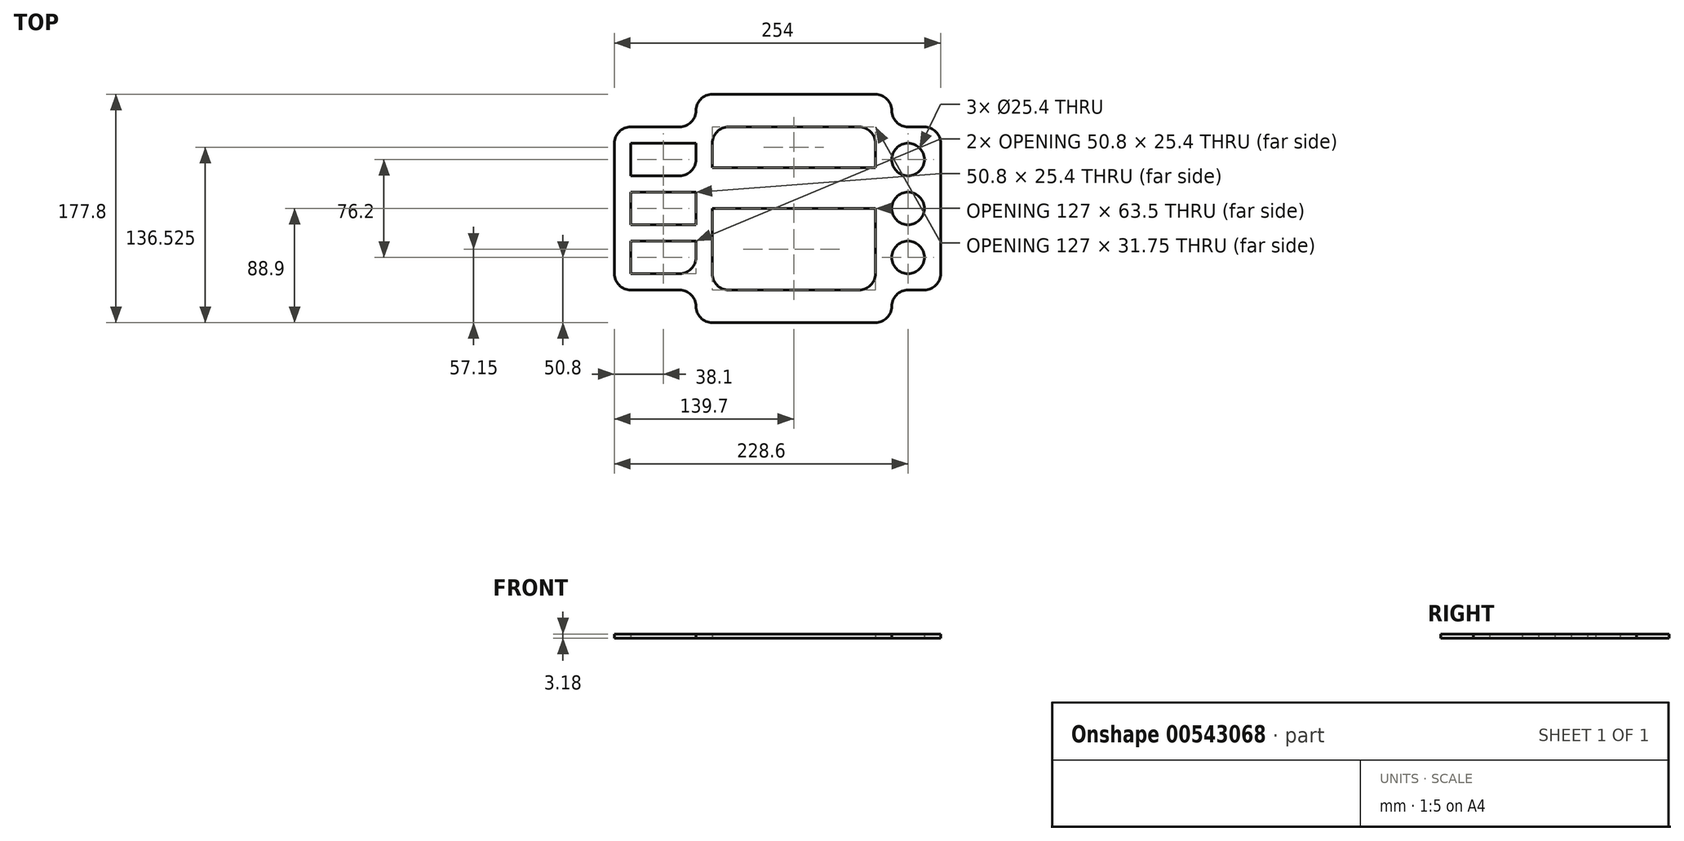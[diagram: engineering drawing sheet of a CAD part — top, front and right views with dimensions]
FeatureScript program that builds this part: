
annotation { "Feature Type Name" : "Feature", "Feature Type Description" : "" }
export const myFeature = defineFeature(function(context is Context, id is Id, definition is map)
    precondition{}
    {
        {
            var Q0;
            Q0=qCreatedBy(makeId("Top.planeOp"),FACE);
            var sketch = newSketch(context, id + "F0", { "sketchPlane" : qUnion([Q0])});
            skLineSegment(sketch, "E0", {"start": v(0, 12.7) * mm, "end": v(0, 12.7) * mm});
            skLineSegment(sketch, "E1", {"start": v(-12.7, 25.4) * mm, "end": v(-50.8, 25.4) * mm});
            skLineSegment(sketch, "E2", {"start": v(-63.5, 38.1) * mm, "end": v(-63.5, 139.7) * mm});
            skLineSegment(sketch, "E3", {"start": v(-50.8, 152.4) * mm, "end": v(-12.7, 152.4) * mm});
            skLineSegment(sketch, "E4", {"start": v(0, 165.1) * mm, "end": v(0, 165.1) * mm});
            skLineSegment(sketch, "E5", {"start": v(12.7, 177.8) * mm, "end": v(139.7, 177.8) * mm});
            skLineSegment(sketch, "E6", {"start": v(152.4, 165.1) * mm, "end": v(152.4, 165.1) * mm});
            skLineSegment(sketch, "E7", {"start": v(165.1, 152.4) * mm, "end": v(177.8, 152.4) * mm});
            skLineSegment(sketch, "E8", {"start": v(190.5, 139.7) * mm, "end": v(190.5, 38.1) * mm});
            skLineSegment(sketch, "E9", {"start": v(177.8, 25.4) * mm, "end": v(165.1, 25.4) * mm});
            skLineSegment(sketch, "E10", {"start": v(152.4, 12.7) * mm, "end": v(152.4, 12.7) * mm});
            skLineSegment(sketch, "E11", {"start": v(139.7, 0) * mm, "end": v(12.7, 0) * mm});
            skPoint(sketch, "E12.visualSharp", {"position": v(0, 25.4) * mm});
            skArc(sketch, "E12.filletArc", {"start": v(0, 12.7) * mm, "mid": v(-3.72, 21.68) * mm, "end": v(-12.7, 25.4) * mm});
            skPoint(sketch, "E13.visualSharp", {"position": v(0, 0) * mm});
            skArc(sketch, "E13.filletArc", {"start": v(0, 12.7) * mm, "mid": v(3.72, 3.72) * mm, "end": v(12.7, 0) * mm});
            skPoint(sketch, "E14.visualSharp", {"position": v(-63.5, 25.4) * mm});
            skArc(sketch, "E14.filletArc", {"start": v(-63.5, 38.1) * mm, "mid": v(-59.78, 29.12) * mm, "end": v(-50.8, 25.4) * mm});
            skPoint(sketch, "E15.visualSharp", {"position": v(-63.5, 152.4) * mm});
            skArc(sketch, "E15.filletArc", {"start": v(-50.8, 152.4) * mm, "mid": v(-59.78, 148.68) * mm, "end": v(-63.5, 139.7) * mm});
            skPoint(sketch, "E16.visualSharp", {"position": v(0, 152.4) * mm});
            skArc(sketch, "E16.filletArc", {"start": v(-12.7, 152.4) * mm, "mid": v(-3.72, 156.12) * mm, "end": v(0, 165.1) * mm});
            skPoint(sketch, "E17.visualSharp", {"position": v(0, 177.8) * mm});
            skArc(sketch, "E17.filletArc", {"start": v(12.7, 177.8) * mm, "mid": v(3.72, 174.08) * mm, "end": v(0, 165.1) * mm});
            skPoint(sketch, "E18.visualSharp", {"position": v(152.4, 177.8) * mm});
            skArc(sketch, "E18.filletArc", {"start": v(152.4, 165.1) * mm, "mid": v(148.68, 174.08) * mm, "end": v(139.7, 177.8) * mm});
            skLineSegment(sketch, "E19", {"start": v(165.1, 152.4) * mm, "end": v(165.1, 25.4) * mm, "construction": true});
            skCircle(sketch, "E20", {"center": v(165.1, 127) * mm, "radius": 12.7 * mm});
            skCircle(sketch, "E21", {"center": v(165.1, 88.9) * mm, "radius": 12.7 * mm});
            skCircle(sketch, "E22", {"center": v(165.1, 50.8) * mm, "radius": 12.7 * mm});
            skPoint(sketch, "E23.visualSharp", {"position": v(152.4, 25.4) * mm});
            skArc(sketch, "E23.filletArc", {"start": v(165.1, 25.4) * mm, "mid": v(156.12, 21.68) * mm, "end": v(152.4, 12.7) * mm});
            skPoint(sketch, "E24.visualSharp", {"position": v(152.4, 0) * mm});
            skArc(sketch, "E24.filletArc", {"start": v(139.7, 0) * mm, "mid": v(148.68, 3.72) * mm, "end": v(152.4, 12.7) * mm});
            skPoint(sketch, "E25.visualSharp", {"position": v(190.5, 25.4) * mm});
            skArc(sketch, "E25.filletArc", {"start": v(177.8, 25.4) * mm, "mid": v(186.78, 29.12) * mm, "end": v(190.5, 38.1) * mm});
            skPoint(sketch, "E26.visualSharp", {"position": v(190.5, 152.4) * mm});
            skArc(sketch, "E26.filletArc", {"start": v(190.5, 139.7) * mm, "mid": v(186.78, 148.68) * mm, "end": v(177.8, 152.4) * mm});
            skPoint(sketch, "E27.visualSharp", {"position": v(152.4, 152.4) * mm});
            skArc(sketch, "E27.filletArc", {"start": v(152.4, 165.1) * mm, "mid": v(156.12, 156.12) * mm, "end": v(165.1, 152.4) * mm});
            skLineSegment(sketch, "E28.bottom", {"start": v(25.4, 152.4) * mm, "end": v(127, 152.4) * mm});
            skLineSegment(sketch, "E28.top", {"start": v(12.7, 120.65) * mm, "end": v(139.7, 120.65) * mm});
            skLineSegment(sketch, "E28.left", {"start": v(12.7, 139.7) * mm, "end": v(12.7, 120.65) * mm});
            skLineSegment(sketch, "E28.right", {"start": v(139.7, 139.7) * mm, "end": v(139.7, 120.65) * mm});
            skPoint(sketch, "E29.visualSharp", {"position": v(12.7, 152.4) * mm});
            skArc(sketch, "E29.filletArc", {"start": v(25.4, 152.4) * mm, "mid": v(16.42, 148.68) * mm, "end": v(12.7, 139.7) * mm});
            skPoint(sketch, "E30.visualSharp", {"position": v(139.7, 152.4) * mm});
            skArc(sketch, "E30.filletArc", {"start": v(139.7, 139.7) * mm, "mid": v(135.98, 148.68) * mm, "end": v(127, 152.4) * mm});
            skLineSegment(sketch, "E31.bottom", {"start": v(12.7, 88.9) * mm, "end": v(139.7, 88.9) * mm});
            skLineSegment(sketch, "E31.top", {"start": v(25.4, 25.4) * mm, "end": v(127, 25.4) * mm});
            skLineSegment(sketch, "E31.left", {"start": v(12.7, 88.9) * mm, "end": v(12.7, 38.1) * mm});
            skLineSegment(sketch, "E31.right", {"start": v(139.7, 88.9) * mm, "end": v(139.7, 38.1) * mm});
            skPoint(sketch, "E32.visualSharp", {"position": v(12.7, 25.4) * mm});
            skArc(sketch, "E32.filletArc", {"start": v(12.7, 38.1) * mm, "mid": v(16.42, 29.12) * mm, "end": v(25.4, 25.4) * mm});
            skPoint(sketch, "E33.visualSharp", {"position": v(139.7, 25.4) * mm});
            skArc(sketch, "E33.filletArc", {"start": v(127, 25.4) * mm, "mid": v(135.98, 29.12) * mm, "end": v(139.7, 38.1) * mm});
            skLineSegment(sketch, "E34.bottom", {"start": v(-50.8, 139.7) * mm, "end": v(0, 139.7) * mm});
            skLineSegment(sketch, "E34.top", {"start": v(-50.8, 114.3) * mm, "end": v(-12.7, 114.3) * mm});
            skLineSegment(sketch, "E34.left", {"start": v(-50.8, 139.7) * mm, "end": v(-50.8, 114.3) * mm});
            skLineSegment(sketch, "E34.right", {"start": v(0, 139.7) * mm, "end": v(0, 127) * mm});
            skLineSegment(sketch, "E35.bottom", {"start": v(-50.8, 101.6) * mm, "end": v(0, 101.6) * mm});
            skLineSegment(sketch, "E35.top", {"start": v(-50.8, 76.2) * mm, "end": v(0, 76.2) * mm});
            skLineSegment(sketch, "E35.left", {"start": v(-50.8, 101.6) * mm, "end": v(-50.8, 76.2) * mm});
            skLineSegment(sketch, "E35.right", {"start": v(0, 101.6) * mm, "end": v(0, 76.2) * mm});
            skLineSegment(sketch, "E36", {"start": v(-50.8, 88.9) * mm, "end": v(0, 88.9) * mm, "construction": true});
            skLineSegment(sketch, "E37.MirrorCS", {"start": v(-50.8, 38.1) * mm, "end": v(-12.7, 38.1) * mm});
            skLineSegment(sketch, "E38.MirrorCS", {"start": v(-50.8, 38.1) * mm, "end": v(-50.8, 63.5) * mm});
            skLineSegment(sketch, "E39.MirrorCS", {"start": v(-50.8, 63.5) * mm, "end": v(0, 63.5) * mm});
            skLineSegment(sketch, "E40.MirrorCS", {"start": v(0, 50.8) * mm, "end": v(0, 63.5) * mm});
            skPoint(sketch, "E41.visualSharp", {"position": v(0, 114.3) * mm});
            skArc(sketch, "E41.filletArc", {"start": v(-12.7, 114.3) * mm, "mid": v(-3.72, 118.02) * mm, "end": v(0, 127) * mm});
            skPoint(sketch, "E42.visualSharp", {"position": v(0, 38.1) * mm});
            skArc(sketch, "E42.filletArc", {"start": v(-12.7, 38.1) * mm, "mid": v(-3.72, 41.82) * mm, "end": v(0, 50.8) * mm});
            skSolve(sketch);
        }
        {
            var Q0;
            Q0=makeQuery(id+"F0.imprint","IMPRINT",FACE,{"disambiguationData":[TD([[makeQuery(id+"F0.imprint","IMPRINT",EDGE,{"derivedFrom":sQuery(id+"F0.wireOp",EDGE,"E1")}),-1.0]])]});
            extrude(context, id + "F1", {"entities" : qUnion([Q0]), "depth" : 3.17 * mm, "offsetDistance" : 25.4 * mm});
        }
    });
